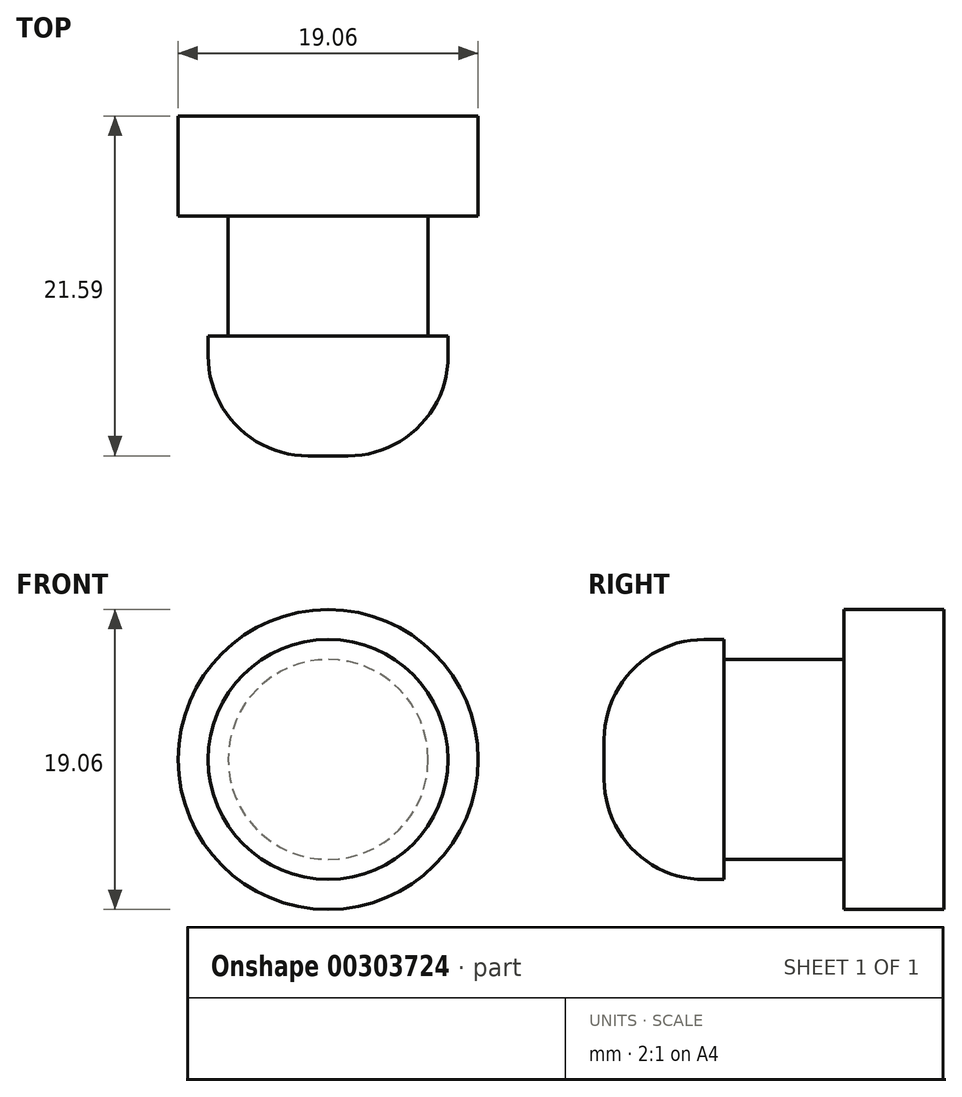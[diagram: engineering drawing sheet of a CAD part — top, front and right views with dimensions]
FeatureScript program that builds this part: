
annotation { "Feature Type Name" : "Feature", "Feature Type Description" : "" }
export const myFeature = defineFeature(function(context is Context, id is Id, definition is map)
    precondition{}
    {
        {
            var Q0;
            Q0=qCreatedBy(makeId("Front.planeOp"),FACE);
            var sketch = newSketch(context, id + "F0", { "sketchPlane" : qUnion([Q0])});
            skCircle(sketch, "E0", {"center": v(0, 0) * mm, "radius": 9.53 * mm});
            skSolve(sketch);
        }
        {
            var Q0;
            Q0 = qSketchRegion(id + "F0", true);
            extrude(context, id + "F1", {"entities" : qUnion([Q0]), "depth" : 6.35 * mm});
        }
        {
            var Q0;
            Q0=makeQuery(id+"F1.opExtrude","CAP_FACE",FACE,{"disambiguationData":[OSD([sQuery(id+"F0.wireOp",EDGE,"E0")])],"isStart":false});
            var sketch = newSketch(context, id + "F2", { "sketchPlane" : qUnion([Q0])});
            skCircle(sketch, "E1", {"center": v(0, 0) * mm, "radius": 6.35 * mm});
            skSolve(sketch);
        }
        {
            var Q0;
            Q0 = qSketchRegion(id + "F2", true);
            extrude(context, id + "F3", {"entities" : qUnion([Q0]), "operationType" : NewBodyOperationType.ADD, "depth" : 7.62 * mm});
        }
        {
            var Q0;
            Q0=makeQuery(id+"F3.opExtrude","CAP_FACE",FACE,{"disambiguationData":[OSD([sQuery(id+"F2.wireOp",EDGE,"E1")])],"isStart":false});
            var sketch = newSketch(context, id + "F4", { "sketchPlane" : qUnion([Q0])});
            skCircle(sketch, "E2", {"center": v(0, 0) * mm, "radius": 7.62 * mm});
            skSolve(sketch);
        }
        {
            var Q0;
            Q0 = qSketchRegion(id + "F4", true);
            extrude(context, id + "F5", {"entities" : qUnion([Q0]), "operationType" : NewBodyOperationType.ADD, "depth" : 7.62 * mm});
        }
        {
            var Q0;
            Q0=makeQuery(id+"F5.opExtrude","CAP_EDGE",EDGE,{"disambiguationData":[OSD([sQuery(id+"F4.wireOp",EDGE,"E2")])],"isStart":false});
            fillet(context, id + "F6", {"entities" : qUnion([Q0]), "radius" : 6.35 * mm, "tangentPropagation" : true, "allowEdgeOverflow" : false});
        }
    });
